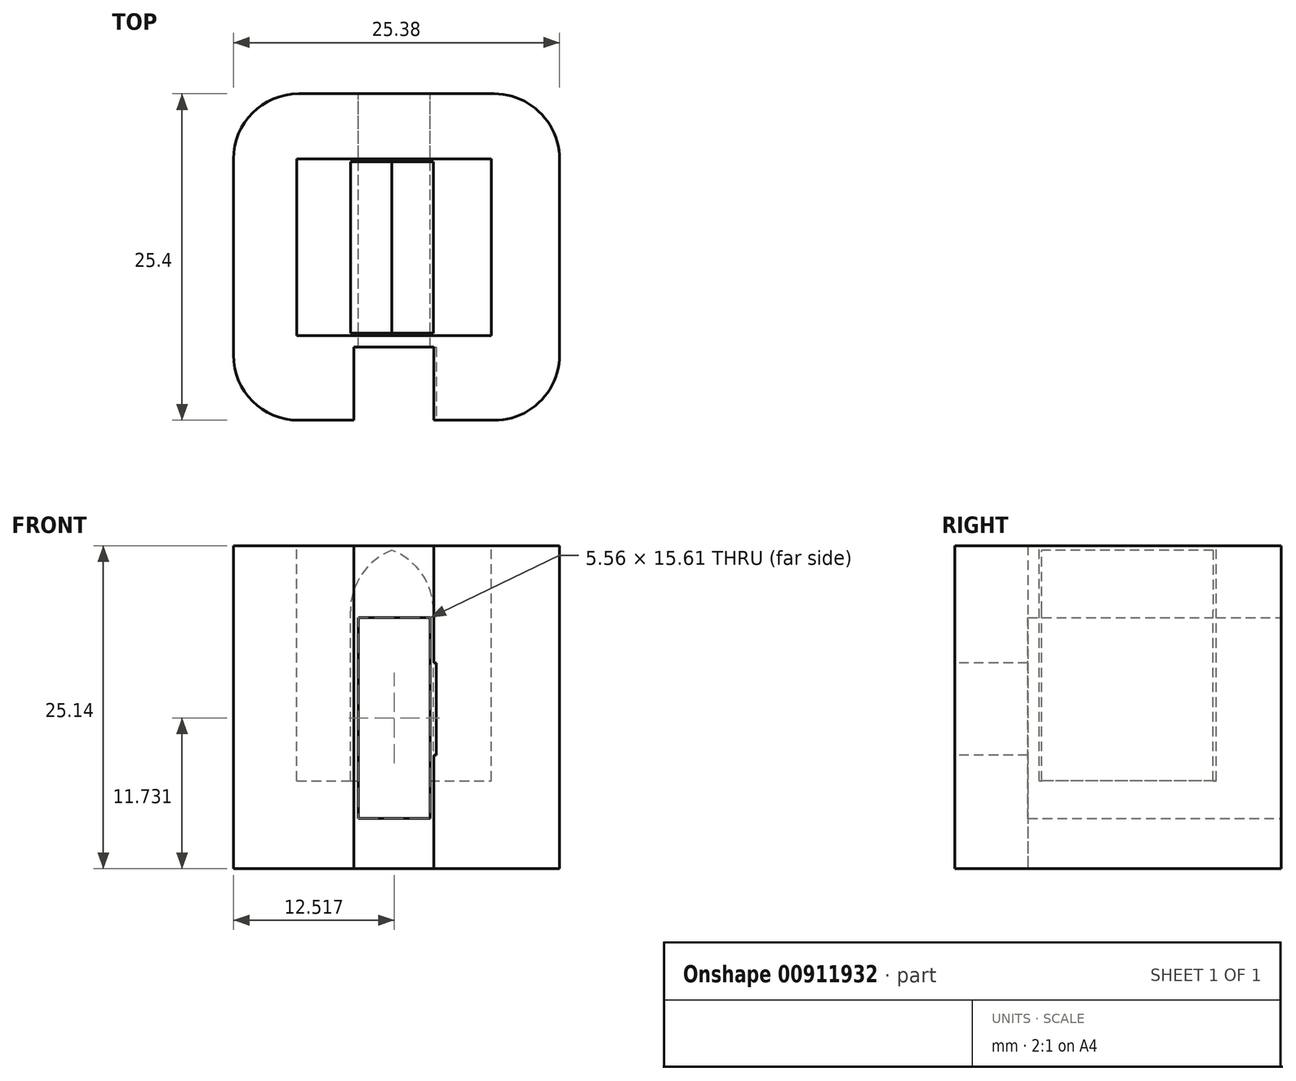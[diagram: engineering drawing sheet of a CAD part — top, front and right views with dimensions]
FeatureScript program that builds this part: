
annotation { "Feature Type Name" : "Feature", "Feature Type Description" : "" }
export const myFeature = defineFeature(function(context is Context, id is Id, definition is map)
    precondition{}
    {
        {
            var Q0;
            Q0=qCreatedBy(makeId("Front.planeOp"),FACE);
            var sketch = newSketch(context, id + "F0", { "sketchPlane" : qUnion([Q0])});
            skLineSegment(sketch, "E0", {"start": v(0, 0) * mm, "end": v(25.37, 0) * mm});
            skLineSegment(sketch, "E1", {"start": v(0, 0) * mm, "end": v(0, 25.14) * mm});
            skLineSegment(sketch, "E2", {"start": v(0, 25.14) * mm, "end": v(25.38, 25.14) * mm});
            skLineSegment(sketch, "E3", {"start": v(25.38, 25.14) * mm, "end": v(25.37, 0) * mm});
            skSolve(sketch);
        }
        {
            var Q0;
            Q0 = qSketchRegion(id + "F0", true);
            extrude(context, id + "F1", {"entities" : qUnion([Q0]), "depth" : 25.4 * mm, "offsetDistance" : 25.4 * mm});
        }
        {
            var Q0;
            Q0=makeQuery(id+"F1.opExtrude","SWEPT_FACE",FACE,{"disambiguationData":[OSD([sQuery(id+"F0.wireOp",EDGE,"E2")])]});
            var sketch = newSketch(context, id + "F2", { "sketchPlane" : qUnion([Q0])});
            skLineSegment(sketch, "E4", {"start": v(4.94, -5.05) * mm, "end": v(4.94, -18.83) * mm});
            skLineSegment(sketch, "E5", {"start": v(4.94, -18.83) * mm, "end": v(20.09, -18.83) * mm});
            skLineSegment(sketch, "E6", {"start": v(4.94, -5.05) * mm, "end": v(20.09, -5.05) * mm});
            skLineSegment(sketch, "E7", {"start": v(20.09, -5.05) * mm, "end": v(20.09, -18.83) * mm});
            skSolve(sketch);
        }
        {
            var Q0;
            Q0 = qSketchRegion(id + "F2", true);
            extrude(context, id + "F3", {"entities" : qUnion([Q0]), "operationType" : NewBodyOperationType.REMOVE, "oppositeDirection" : true, "depth" : 18.29 * mm, "offsetDistance" : 25.4 * mm});
        }
        {
            var Q0;
            Q0=makeQuery(id+"F2.imprint","IMPRINT",FACE,{"disambiguationData":[TD([[makeQuery(id+"F2.imprint","IMPRINT",EDGE,{"derivedFrom":sQuery(id+"F2.wireOp",EDGE,"E4")}),1.0]])]});
            var sketch = newSketch(context, id + "F4", { "sketchPlane" : qUnion([Q0])});
            skLineSegment(sketch, "E8.bottom", {"start": v(9.1, -5.3) * mm, "end": v(15.57, -5.3) * mm});
            skLineSegment(sketch, "E8.top", {"start": v(9.1, -18.62) * mm, "end": v(15.57, -18.62) * mm});
            skLineSegment(sketch, "E8.left", {"start": v(9.1, -5.3) * mm, "end": v(9.1, -18.62) * mm});
            skLineSegment(sketch, "E8.right", {"start": v(15.57, -5.3) * mm, "end": v(15.57, -18.62) * mm});
            skSolve(sketch);
        }
        {
            var Q0;
            Q0 = qSketchRegion(id + "F4", true);
            extrude(context, id + "F5", {"entities" : qUnion([Q0]), "operationType" : NewBodyOperationType.ADD, "oppositeDirection" : true, "depth" : 22.4 * mm, "offsetDistance" : 25.4 * mm});
        }
        {
            var Q0;
            Q0=makeQuery(id+"F1.opExtrude","CAP_FACE",FACE,{"disambiguationData":[OSD([sQuery(id+"F0.wireOp",EDGE,"E0"),sQuery(id+"F0.wireOp",EDGE,"E1"),sQuery(id+"F0.wireOp",EDGE,"E2"),sQuery(id+"F0.wireOp",EDGE,"E3")])],"isStart":false});
            var sketch = newSketch(context, id + "F6", { "sketchPlane" : qUnion([Q0])});
            skLineSegment(sketch, "E9.bottom", {"start": v(9.38, 25.14) * mm, "end": v(15.6, 25.14) * mm});
            skLineSegment(sketch, "E9.top", {"start": v(9.38, 0) * mm, "end": v(15.6, 0) * mm});
            skLineSegment(sketch, "E9.left", {"start": v(9.38, 25.14) * mm, "end": v(9.38, 0) * mm});
            skLineSegment(sketch, "E9.right", {"start": v(15.6, 25.14) * mm, "end": v(15.6, 0) * mm});
            skSolve(sketch);
        }
        {
            var Q0;
            Q0=makeQuery(id+"F1.opExtrude","CAP_EDGE",EDGE,{"disambiguationData":[OSD([sQuery(id+"F0.wireOp",EDGE,"E1")])],"isStart":false});
            var Q1;
            Q1=makeQuery(id+"F1.opExtrude","CAP_EDGE",EDGE,{"disambiguationData":[OSD([sQuery(id+"F0.wireOp",EDGE,"E3")])],"isStart":false});
            var Q2;
            Q2=makeQuery(id+"F1.opExtrude","CAP_EDGE",EDGE,{"disambiguationData":[OSD([sQuery(id+"F0.wireOp",EDGE,"E3")])],"isStart":true});
            var Q3;
            Q3=makeQuery(id+"F1.opExtrude","CAP_EDGE",EDGE,{"disambiguationData":[OSD([sQuery(id+"F0.wireOp",EDGE,"E1")])],"isStart":true});
            var Q4;
            Q4=makeQuery(id+"F5.opExtrude","CAP_EDGE",EDGE,{"disambiguationData":[OSD([sQuery(id+"F4.wireOp",EDGE,"E8.left")])],"isStart":true});
            var Q5;
            Q5=makeQuery(id+"F5.opExtrude","CAP_EDGE",EDGE,{"disambiguationData":[OSD([sQuery(id+"F4.wireOp",EDGE,"E8.right")])],"isStart":true});
            fillet(context, id + "F7", {"entities" : qUnion([Q0, Q1, Q2, Q3, Q4, Q5]), "radius" : 5.08 * mm, "tangentPropagation" : true, "allowEdgeOverflow" : false});
        }
        {
            var Q0;
            Q0=makeQuery(id+"F6.imprint","IMPRINT",FACE,{"disambiguationData":[TD([[makeQuery(id+"F6.imprint","IMPRINT",EDGE,{"derivedFrom":sQuery(id+"F6.wireOp",EDGE,"E9.bottom")}),-1.0]])]});
            var sketch = newSketch(context, id + "F8", { "sketchPlane" : qUnion([Q0])});
            skLineSegment(sketch, "E10", {"start": v(9.41, 16.01) * mm, "end": v(15.78, 16.01) * mm});
            skLineSegment(sketch, "E11", {"start": v(15.78, 16.01) * mm, "end": v(15.78, 8.85) * mm});
            skLineSegment(sketch, "E12", {"start": v(15.78, 8.85) * mm, "end": v(9.41, 8.85) * mm});
            skLineSegment(sketch, "E13", {"start": v(9.41, 8.85) * mm, "end": v(9.41, 16.01) * mm});
            skSolve(sketch);
        }
        {
            var Q0;
            {var subQ0=sQuery(id+"F8.wireOp",EDGE,"E11");Q0=makeQuery(id+"F8.imprint","IMPRINT",FACE,{"disambiguationData":[TD([[makeQuery(id+"F8.imprint","IMPRINT",EDGE,{"derivedFrom":subQ0}),-1.0]])]});}
            var Q1;
            Q1=makeQuery(id+"F6.imprint","IMPRINT",FACE,{"disambiguationData":[TD([[makeQuery(id+"F6.imprint","IMPRINT",EDGE,{"derivedFrom":sQuery(id+"F6.wireOp",EDGE,"E9.bottom")}),-1.0]])]});
            extrude(context, id + "F9", {"entities" : qUnion([Q0, Q1]), "operationType" : NewBodyOperationType.REMOVE, "oppositeDirection" : true, "depth" : 5.7 * mm, "offsetDistance" : 25.4 * mm});
        }
        {
            var Q0;
            Q0=makeQuery(id+"F0.imprint","IMPRINT",FACE,{"disambiguationData":[TD([[makeQuery(id+"F0.imprint","IMPRINT",EDGE,{"derivedFrom":sQuery(id+"F0.wireOp",EDGE,"E0")}),1.0]])]});
            var sketch = newSketch(context, id + "F10", { "sketchPlane" : qUnion([Q0])});
            skLineSegment(sketch, "E14", {"start": v(15.3, 15.52) * mm, "end": v(15.3, 19.54) * mm});
            skLineSegment(sketch, "E15", {"start": v(15.3, 19.54) * mm, "end": v(9.73, 19.54) * mm});
            skLineSegment(sketch, "E16", {"start": v(9.73, 19.54) * mm, "end": v(9.73, 3.92) * mm});
            skLineSegment(sketch, "E17", {"start": v(15.3, 15.52) * mm, "end": v(15.3, 3.92) * mm});
            skLineSegment(sketch, "E18", {"start": v(15.3, 3.92) * mm, "end": v(9.73, 3.92) * mm});
            skSolve(sketch);
        }
        {
            var Q0;
            Q0=makeQuery(id+"F10.imprint","IMPRINT",FACE,{"disambiguationData":[TD([[makeQuery(id+"F10.imprint","IMPRINT",EDGE,{"derivedFrom":sQuery(id+"F10.wireOp",EDGE,"E14")}),1.0]])]});
            extrude(context, id + "F11", {"entities" : qUnion([Q0]), "operationType" : NewBodyOperationType.REMOVE, "depth" : 65.18 * mm, "offsetDistance" : 25.4 * mm});
        }
    });
